# Revit family: METEOR_Atria II 8_REVIT_File (Standard)
name_source: partatom
category: Lighting Fixtures
revit_build: Autodesk Revit 2017 (Build: 20160225_1515(x64)
units: mm (PartAtom-declared; Revit-internal decimal feet)

## family parameters
Always vertical = Yes
Cut with Voids When Loaded = No
Light Source = Yes
OmniClass Number = 23.80.70.00
OmniClass Title = Lighting
Part Type = Normal
Room Calculation Point = No
Round Connector Dimension = Use Diameter
Shared = No
Work Plane-Based = No

## types (64) — shared parameters
Color Filter = 16777215
Dimming Lamp Color Temperature Shift = <None>
Tilt Angle = 90.00°

## per-type parameters (varying)
| type | Photometric Web File |
| ASII8-80W-278-30D | ASII8-80W-278-30D.ies |
| ASII8-80W-278-45D | ASII8-80W-278-45D.ies |
| ASII8-80W-278-55D | ASII8-80W-278-55D.ies |
| ASII8-80W-278-WD | ASII8-80W-278-WD.ies |
| ASII8-80W-308-30D | ASII8-80W-308-30D.ies |
| ASII8-80W-308-45D | ASII8-80W-308-45D.ies |
| ASII8-80W-308-55D | ASII8-80W-308-55D.ies |
| ASII8-80W-308-WD | ASII8-80W-308-WD.ies |
| ASII8-80W-358-30D | ASII8-80W-358-30D.ies |
| ASII8-80W-358-45D | ASII8-80W-358-45D.ies |
| ASII8-80W-358-55D | ASII8-80W-358-55D.ies |
| ASII8-80W-358-WD | ASII8-80W-358-WD.ies |
| ASII8-80W-408-30D | ASII8-80W-408-30D.ies |
| ASII8-80W-408-45D | ASII8-80W-408-45D.ies |
| ASII8-80W-408-55D | ASII8-80W-408-55D.ies |
| ASII8-80W-408-WD | ASII8-80W-408-WD.ies |
| ASII8-100W-278-30D | ASII8-100W-278-30D.ies |
| ASII8-100W-278-45D | ASII8-100W-278-45D.ies |
| ASII8-100W-278-55D | ASII8-100W-278-55D.ies |
| ASII8-100W-278-WD | ASII8-100W-278-WD.ies |
| ASII8-100W-308-30D | ASII8-100W-308-30D.ies |
| ASII8-100W-308-45D | ASII8-100W-308-45D.ies |
| ASII8-100W-308-55D | ASII8-80W-308-55D.ies |
| ASII8-100W-308-WD | ASII8-100W-308-WD.ies |
| ASII8-100W-358-30D | ASII8-100W-358-30D.ies |
| ASII8-100W-358-45D | ASII8-100W-358-45D.ies |
| ASII8-100W-358-55D | ASII8-100W-358-55D.ies |
| ASII8-100W-358-WD | ASII8-100W-358-WD.ies |
| ASII8-100W-408-30D | ASII8-100W-408-30D.ies |
| ASII8-100W-408-45D | ASII8-100W-408-45D.ies |
| ASII8-100W-408-55D | ASII8-100W-408-55D.ies |
| ASII8-100W-408-WD | ASII8-100W-408-WD.ies |
| ASII8-130W-278-30D | ASII8-130W-278-30D.ies |
| ASII8-130W-278-45D | ASII8-130W-278-45D.ies |
| ASII8-130W-278-55D | ASII8-130W-278-55D.ies |
| ASII8-130W-278-WD | ASII8-130W-278-WD.ies |
| ASII8-130W-308-30D | ASII8-130W-308-30D.ies |
| ASII8-130W-308-45D | ASII8-130W-308-45D.ies |
| ASII8-130W-308-55D | ASII8-130W-308-55D.ies |
| ASII8-130W-308-WD | ASII8-130W-308-WD.ies |
| ASII8-130W-358-30D | ASII8-130W-358-30D.ies |
| ASII8-130W-358-45D | ASII8-130W-358-45D.ies |
| ASII8-130W-358-55D | ASII8-130W-358-55D.ies |
| ASII8-130W-358-WD | ASII8-130W-358-WD.ies |
| ASII8-130W-408-30D | ASII8-130W-408-30D.ies |
| ASII8-130W-408-45D | ASII8-130W-408-45D.ies |
| ASII8-130W-408-55D | ASII8-130W-408-55D.ies |
| ASII8-130W-408-WD | ASII8-130W-408-WD.ies |
| ASII8-160W-278-30D | ASII8-160W-278-30D.ies |
| ASII8-160W-278-45D | ASII8-160W-278-45D.ies |
| ASII8-160W-278-55D | ASII8-160W-278-55D.ies |
| ASII8-160W-278-WD | ASII8-160W-278-WD.ies |
| ASII8-160W-308-30D | ASII8-160W-308-30D.ies |
| ASII8-160W-308-45D | ASII8-160W-308-45D.ies |
| ASII8-160W-308-55D | ASII8-160W-308-55D.ies |
| ASII8-160W-308-WD | ASII8-160W-308-WD.ies |
| ASII8-160W-358-30D | ASII8-160W-358-30D.ies |
| ASII8-160W-358-45D | ASII8-160W-358-45D.ies |
| ASII8-160W-358-55D | ASII8-160W-358-55D.ies |
| ASII8-160W-358-WD | ASII8-160W-358-WD.ies |
| ASII8-160W-408-30D | ASII8-160W-408-30D.ies |
| ASII8-160W-408-45D | ASII8-160W-408-45D.ies |
| ASII8-160W-408-55D | ASII8-160W-408-55D.ies |
| ASII8-160W-408-WD | ASII8-160W-408-WD.ies |

## geometry (parser evidence)
native form markers: Sweep x2
no freeform markers — native parametric forms only
